# Revit family: WC AUSTRAL P
name_source: partatom
category: Aparatos sanitarios
units: mm (PartAtom-declared; Revit-internal decimal feet)

## family parameters
Compartido = Sí
Corte con vacíos al cargar = No
Cota de conector redondo = Diámetro de uso
Número OmniClass = 23.45.00.00
Punto de cálculo de habitación = No
Se basa en plano de trabajo = Sí
Siempre vertical = Sí
Tipo de pieza = Normal
Título OmniClass = Sanitary, Laundry, and Cleaning Equipment

## types (1)
- WC AUSTRAL P
    Accessories = Sistema de sujeción al piso
    Cerámica = Cerámica porcelanizada de alto brillo. Calidad "A", tipo I
    Conexión de Alimentación = A la alimentacion Ø15/16-14 NS-1
    Conexión de Descarga = A la descarga se acopla al Ø de drenaje de 4" con brida sanitaria o cuello de cera.
    Elevación por defecto = 0.0"
    Fabricante = Helvex S.A. de C.V.
    Guía de instalación = https://www.helvex.com.mx
    Hoja de Especificación = https://www.helvex.com.mx
    Imagen de tipo = product720.jpg
    Modelo = WC AUSTRAL P
    Operation = Accione la Palanca para una descarga de 3,8
litros.
    Presión Máxima de Trabajo = 85.3 psi
    Presión Mínima de Trabajo = 3.6 psi
    URL = https://www.helvex.com.mx
    Valves = Valv. de admisión y descarga certificadas, Valv. de admisión silenciosa, válvulas armadas y calibradas, válvula de descarga con sello hermético, Válvula de descarga de Ø 3" tipo sapo.

## geometry (parser evidence)
native form markers: Sweep x3
no freeform markers — native parametric forms only
